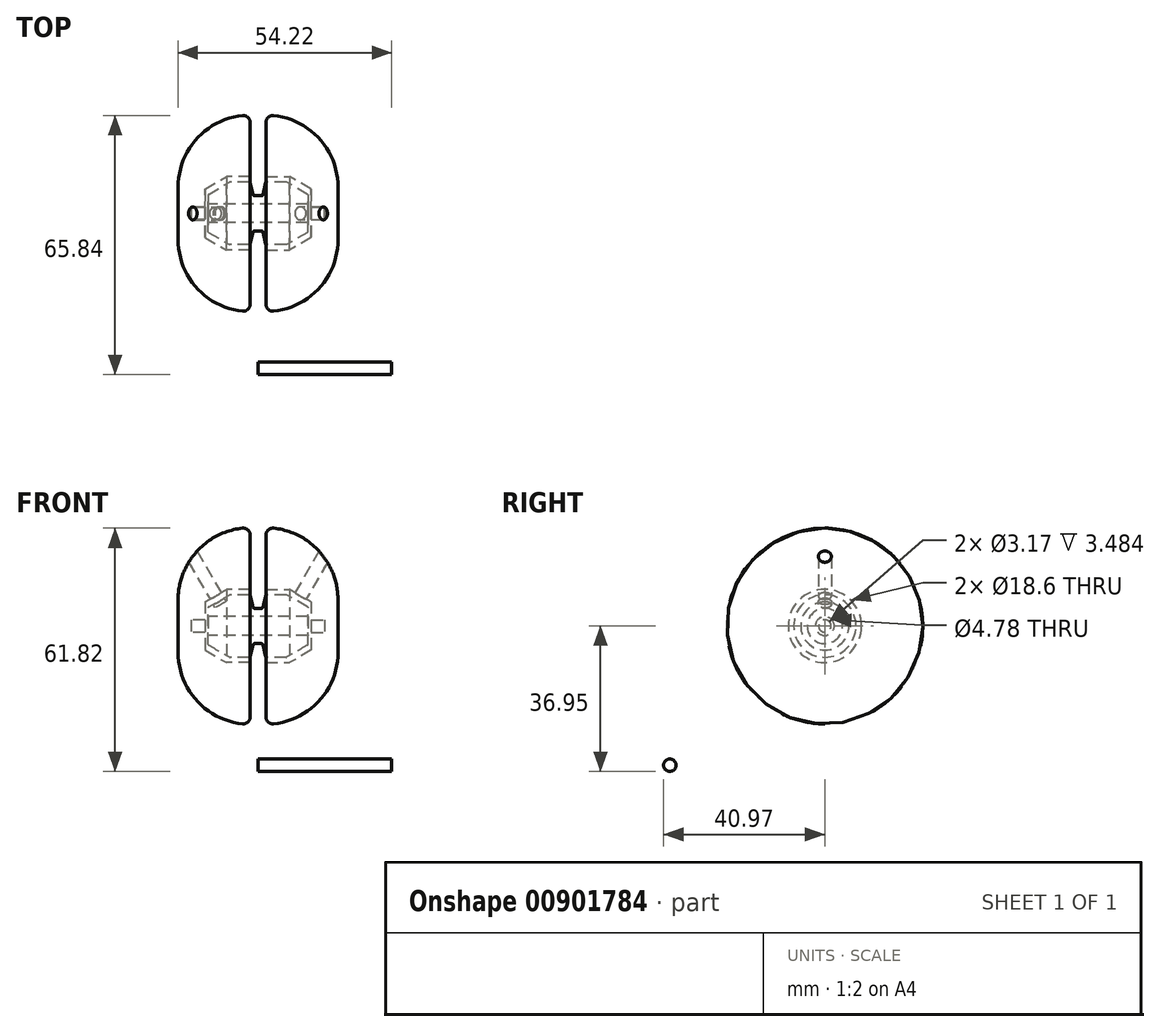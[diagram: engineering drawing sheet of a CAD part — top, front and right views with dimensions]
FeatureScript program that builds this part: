
annotation { "Feature Type Name" : "Feature", "Feature Type Description" : "" }
export const myFeature = defineFeature(function(context is Context, id is Id, definition is map)
    precondition{}
    {
        {
            var Q0;
            Q0=qCreatedBy(makeId("Top.planeOp"),FACE);
            var sketch = newSketch(context, id + "F0", { "sketchPlane" : qUnion([Q0])});
            skLineSegment(sketch, "E0", {"start": v(-43.15, 0) * mm, "end": v(47.7, 0) * mm, "construction": true});
            skLineSegment(sketch, "E1", {"start": v(0, 35.7) * mm, "end": v(0, -27.9) * mm, "construction": true});
            skLineSegment(sketch, "E2", {"start": v(-12.7, 4.76) * mm, "end": v(-7.2, 7.94) * mm});
            skLineSegment(sketch, "E3", {"start": v(-7.2, 7.94) * mm, "end": v(-2, 7.94) * mm});
            skLineSegment(sketch, "E4", {"start": v(7.2, 7.94) * mm, "end": v(12.7, 4.76) * mm});
            skLineSegment(sketch, "E5", {"start": v(-2, 7.94) * mm, "end": v(-1.25, 4.76) * mm});
            skLineSegment(sketch, "E6", {"start": v(-0.9, 4.49) * mm, "end": v(0.9, 4.49) * mm});
            skLineSegment(sketch, "E7", {"start": v(1.25, 4.76) * mm, "end": v(2, 7.94) * mm});
            skLineSegment(sketch, "E8.trimOffspring", {"start": v(2, 7.94) * mm, "end": v(7.2, 7.94) * mm});
            skPoint(sketch, "E9.visualSharp", {"position": v(-1.18, 4.49) * mm});
            skArc(sketch, "E9.filletArc", {"start": v(-1.25, 4.76) * mm, "mid": v(-1.12, 4.57) * mm, "end": v(-0.9, 4.49) * mm});
            skPoint(sketch, "E10.visualSharp", {"position": v(1.18, 4.49) * mm});
            skArc(sketch, "E10.filletArc", {"start": v(0.9, 4.49) * mm, "mid": v(1.12, 4.57) * mm, "end": v(1.25, 4.76) * mm});
            skLineSegment(sketch, "E11", {"start": v(-12.7, 4.76) * mm, "end": v(-12.7, 2.39) * mm});
            skLineSegment(sketch, "E12", {"start": v(12.7, 4.76) * mm, "end": v(12.7, 2.39) * mm});
            skLineSegment(sketch, "E13", {"start": v(-12.7, 2.39) * mm, "end": v(12.7, 2.39) * mm});
            skSolve(sketch);
        }
        {
            var Q0;
            Q0=qSketchRegion(id+"F0",true);
            var Q1;
            Q1=sQuery(id+"F0.wireOp",EDGE,"E0");
            revolve(context, id + "F1", {"surfaceOperationType" : NewSurfaceOperationType.NEW, "entities" : qUnion([Q0]), "axis" : qUnion([Q1]), "revolveType" : RevolveType.FULL});
        }
        {
            var Q0;
            Q0=qCreatedBy(makeId("Front.planeOp"),FACE);
            var sketch = newSketch(context, id + "F2", { "sketchPlane" : qUnion([Q0])});
            skLineSegment(sketch, "E14", {"start": v(-29.24, 0) * mm, "end": v(31.38, 0) * mm, "construction": true});
            skLineSegment(sketch, "E15", {"start": v(-7.2, 7.94) * mm, "end": v(-2, 7.94) * mm});
            skLineSegment(sketch, "E16", {"start": v(-12.69, 4.77) * mm, "end": v(-7.2, 7.94) * mm});
            skLineSegment(sketch, "E17", {"start": v(-7.2, -7.94) * mm, "end": v(-12.36, -4.96) * mm});
            skLineSegment(sketch, "E18", {"start": v(-2, -7.94) * mm, "end": v(-7.2, -7.94) * mm});
            skLineSegment(sketch, "E19.0", {"start": v(-2, -7.94) * mm, "end": v(-2, 7.94) * mm});
            skLineSegment(sketch, "E20", {"start": v(-2, 9.3) * mm, "end": v(-2, 23.1) * mm});
            skLineSegment(sketch, "E21", {"start": v(-20.31, 6.66) * mm, "end": v(-20.31, 0) * mm});
            skLineSegment(sketch, "E22", {"start": v(-20.31, 0) * mm, "end": v(-16.96, 0) * mm});
            skLineSegment(sketch, "E23", {"start": v(-16.96, 0) * mm, "end": v(-16.96, 1.59) * mm});
            skLineSegment(sketch, "E24", {"start": v(-16.96, 1.59) * mm, "end": v(-13.47, 1.59) * mm});
            skLineSegment(sketch, "E25", {"start": v(-13.47, 1.59) * mm, "end": v(-13.47, 6.13) * mm});
            skLineSegment(sketch, "E26", {"start": v(-13.47, 6.13) * mm, "end": v(-7.99, 9.3) * mm});
            skLineSegment(sketch, "E27", {"start": v(-7.99, 9.3) * mm, "end": v(-2, 9.3) * mm});
            skPoint(sketch, "E28.visualSharp", {"position": v(-2, 24.87) * mm});
            skArc(sketch, "E28.filletArc", {"start": v(-2, 23.1) * mm, "mid": v(-2.59, 24.41) * mm, "end": v(-3.97, 24.86) * mm});
            skArc(sketch, "E29", {"start": v(-3.97, 24.86) * mm, "mid": v(-15.63, 18.9) * mm, "end": v(-20.31, 6.66) * mm});
            skPoint(sketch, "E30", {"position": v(-10.73, 7.72) * mm});
            skPoint(sketch, "E31", {"position": v(-9.94, 6.35) * mm});
            skLineSegment(sketch, "E32", {"start": v(-9.94, 6.35) * mm, "end": v(-12.83, 11.35) * mm, "construction": true});
            skLineSegment(sketch, "E33", {"start": v(-9.94, 6.35) * mm, "end": v(-7.94, 2.88) * mm, "construction": true});
            skSolve(sketch);
        }
        {
            var Q0;
            Q0=makeQuery(id+"F2.imprint","IMPRINT",FACE,{"disambiguationData":[TD([[makeQuery(id+"F2.imprint","IMPRINT",EDGE,{"derivedFrom":sQuery(id+"F2.wireOp",EDGE,"E20")}),1.0]])]});
            var Q1;
            Q1=sQuery(id+"F2.wireOp",EDGE,"E22");
            revolve(context, id + "F3", {"surfaceOperationType" : NewSurfaceOperationType.NEW, "entities" : qUnion([Q0]), "axis" : qUnion([Q1]), "revolveType" : RevolveType.FULL});
        }
        {
            var Q0;
            Q0=sQuery(id+"F2.wireOp",EDGE,"E26");
            cPlane(context, id + "F4", {"entities" : qUnion([Q0]), "cplaneType" : CPlaneType.LINE_ANGLE, "offset" : 25.4 * mm, "angle" : 90 * degree, "width" : 152.4 * mm, "height" : 152.4 * mm});
        }
        {
            var Q0;
            Q0=qCreatedBy(id+"F4.planeOp",FACE);
            var sketch = newSketch(context, id + "F5", { "sketchPlane" : qUnion([Q0])});
            skCircle(sketch, "E34", {"center": v(-5.53, 0) * mm, "radius": 1.65 * mm});
            skSolve(sketch);
        }
        {
            var Q0;
            Q0=qSketchRegion(id+"F5",true);
            extrude(context, id + "F6", {"entities" : qUnion([Q0]), "operationType" : NewBodyOperationType.REMOVE, "depth" : 13.36 * mm, "offsetDistance" : 25.4 * mm, "hasSecondDirection" : true, "secondDirectionOppositeDirection" : true, "secondDirectionDepth" : 1.57 * mm});
        }
        {
            var Q0;
            Q0=makeQuery(id+"F3.opRevolve","SWEPT_BODY",BODY,{"disambiguationData":[OSD([sQuery(id+"F2.wireOp",EDGE,"E20"),sQuery(id+"F2.wireOp",EDGE,"E21"),sQuery(id+"F2.wireOp",EDGE,"E22"),sQuery(id+"F2.wireOp",EDGE,"E23"),sQuery(id+"F2.wireOp",EDGE,"E24"),sQuery(id+"F2.wireOp",EDGE,"E25"),sQuery(id+"F2.wireOp",EDGE,"E26"),sQuery(id+"F2.wireOp",EDGE,"E27"),sQuery(id+"F2.wireOp",EDGE,"E28.filletArc"),sQuery(id+"F2.wireOp",EDGE,"E29")])]});
            var Q1;
            Q1=qCreatedBy(makeId("Right.planeOp"),FACE);
            mirror(context, id + "F7", {"entities" : qUnion([Q0]), "mirrorPlane" : qUnion([Q1])});
        }
        {
            var Q0;
            Q0=qCreatedBy(makeId("Right.planeOp"),FACE);
            var sketch = newSketch(context, id + "F8", { "sketchPlane" : qUnion([Q0])});
            skCircle(sketch, "E35", {"center": v(-39.39, -35.37) * mm, "radius": 1.59 * mm});
            skSolve(sketch);
        }
        {
            var Q0;
            Q0=qSketchRegion(id+"F8",true);
            extrude(context, id + "F9", {"entities" : qUnion([Q0]), "depth" : 33.9 * mm, "offsetDistance" : 25.4 * mm});
        }
        {
            var Q0;
            Q0=qCreatedBy(id+"F4.planeOp",FACE);
            cPlane(context, id + "F10", {"entities" : qUnion([Q0]), "cplaneType" : CPlaneType.OFFSET, "offset" : 6.35 * mm, "width" : 152.4 * mm, "height" : 152.4 * mm});
        }
        {
            var Q0;
            Q0=qCreatedBy(id+"F10.planeOp",FACE);
            var sketch = newSketch(context, id + "F11", { "sketchPlane" : qUnion([Q0])});
            skCircle(sketch, "E36", {"center": v(-5.53, 0) * mm, "radius": 1.65 * mm});
            skSolve(sketch);
        }
        {
            var Q0;
            Q0=makeQuery(id+"F11.imprint","IMPRINT",FACE,{"disambiguationData":[TD([[makeQuery(id+"F11.imprint","IMPRINT",EDGE,{"derivedFrom":sQuery(id+"F11.wireOp",EDGE,"E36")}),1.0]])]});
            extrude(context, id + "F12", {"entities" : qUnion([Q0]), "operationType" : NewBodyOperationType.REMOVE, "oppositeDirection" : true, "depth" : 8.94 * mm, "offsetDistance" : 25.4 * mm, "hasSecondDirection" : true, "secondDirectionOppositeDirection" : false, "secondDirectionDepth" : 2.18 * mm});
        }
        {
            var Q0;
            Q0=makeQuery(id+"F1.opRevolve","SWEPT_EDGE",EDGE,{"disambiguationData":[OSD([sQuery(id+"F0.wireOp",EDGE,"E2"),sQuery(id+"F0.wireOp",EDGE,"E11")])]});
            var Q1;
            Q1=makeQuery(id+"F1.opRevolve","SWEPT_EDGE",EDGE,{"disambiguationData":[OSD([sQuery(id+"F0.wireOp",EDGE,"E2"),sQuery(id+"F0.wireOp",EDGE,"E3")])]});
            var Q2;
            Q2=makeQuery(id+"F1.opRevolve","SWEPT_EDGE",EDGE,{"disambiguationData":[OSD([sQuery(id+"F0.wireOp",EDGE,"E3"),sQuery(id+"F0.wireOp",EDGE,"E5")])]});
            var Q3;
            Q3=makeQuery(id+"F1.opRevolve","SWEPT_EDGE",EDGE,{"disambiguationData":[OSD([sQuery(id+"F0.wireOp",EDGE,"E7"),sQuery(id+"F0.wireOp",EDGE,"E8.trimOffspring")])]});
            var Q4;
            Q4=makeQuery(id+"F1.opRevolve","SWEPT_EDGE",EDGE,{"disambiguationData":[OSD([sQuery(id+"F0.wireOp",EDGE,"E4"),sQuery(id+"F0.wireOp",EDGE,"E8.trimOffspring")])]});
            var Q5;
            Q5=makeQuery(id+"F1.opRevolve","SWEPT_EDGE",EDGE,{"disambiguationData":[OSD([sQuery(id+"F0.wireOp",EDGE,"E4"),sQuery(id+"F0.wireOp",EDGE,"E12")])]});
            fillet(context, id + "F13", {"entities" : qUnion([Q0, Q1, Q2, Q3, Q4, Q5]), "radius" : 0.23 * mm, "tangentPropagation" : true, "allowEdgeOverflow" : false});
        }
    });
